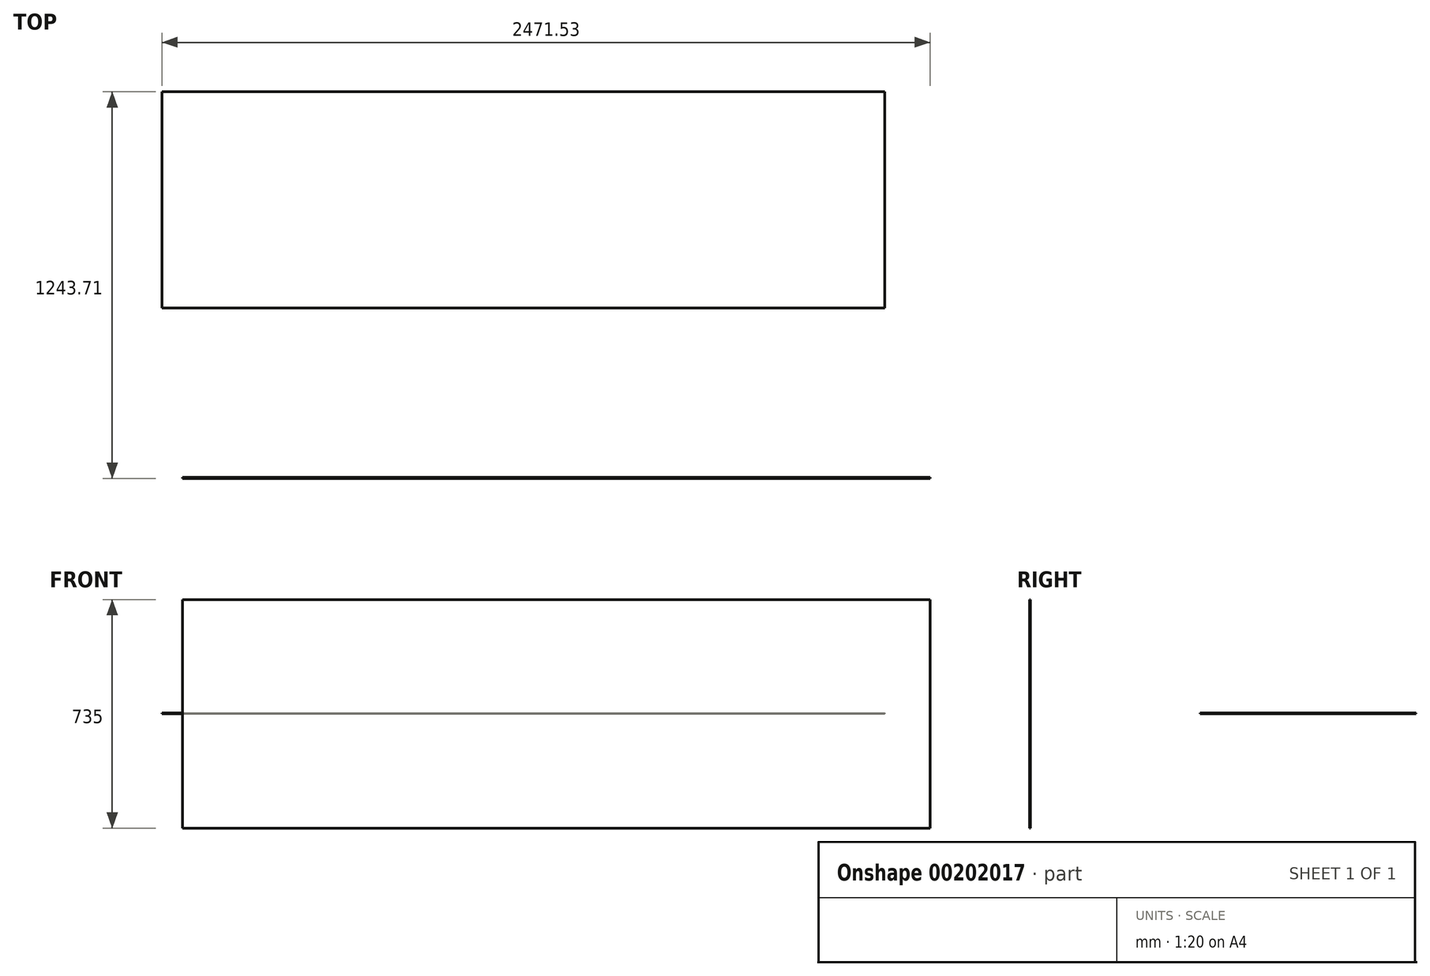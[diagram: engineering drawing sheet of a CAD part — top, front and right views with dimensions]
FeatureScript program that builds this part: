
annotation { "Feature Type Name" : "Feature", "Feature Type Description" : "" }
export const myFeature = defineFeature(function(context is Context, id is Id, definition is map)
    precondition{}
    {
        {
            var Q0;
            Q0=qCreatedBy(makeId("Front.planeOp"),FACE);
            var sketch = newSketch(context, id + "F0", { "sketchPlane" : qUnion([Q0])});
            skLineSegment(sketch, "E0.bottom", {"start": v(1202.5, 367.5) * mm, "end": v(-1202.5, 367.5) * mm});
            skLineSegment(sketch, "E0.top", {"start": v(1202.5, -367.5) * mm, "end": v(-1202.5, -367.5) * mm});
            skLineSegment(sketch, "E0.left", {"start": v(1202.5, 367.5) * mm, "end": v(1202.5, -367.5) * mm});
            skLineSegment(sketch, "E0.right", {"start": v(-1202.5, 367.5) * mm, "end": v(-1202.5, -367.5) * mm});
            skPoint(sketch, "E0.middle", {"position": v(0, 0) * mm});
            skSolve(sketch);
        }
        {
            var Q0;
            Q0=makeQuery(id+"F0.imprint","IMPRINT",FACE,{"disambiguationData":[TD([[makeQuery(id+"F0.imprint","IMPRINT",EDGE,{"derivedFrom":sQuery(id+"F0.wireOp",EDGE,"E0.bottom")}),1.0]])]});
            extrude(context, id + "F1", {"entities" : qUnion([Q0]), "depth" : 3 * mm});
        }
        {
            var Q0;
            Q0=makeQuery(id+"F1.opExtrude","CAP_FACE",FACE,{"disambiguationData":[OSD([sQuery(id+"F0.wireOp",EDGE,"E0.bottom"),sQuery(id+"F0.wireOp",EDGE,"E0.top"),sQuery(id+"F0.wireOp",EDGE,"E0.left"),sQuery(id+"F0.wireOp",EDGE,"E0.right")])],"isStart":false});
            var sketch = newSketch(context, id + "F2", { "sketchPlane" : qUnion([Q0])});
            skLineSegment(sketch, "E1", {"start": v(-1202.5, 17.5) * mm, "end": v(1202.5, 17.5) * mm, "construction": true});
            skPoint(sketch, "E2", {"position": v(0, 17.5) * mm});
            skPoint(sketch, "E3", {"position": v(-1002.5, 17.5) * mm});
            skPoint(sketch, "E4", {"position": v(702.5, 17.5) * mm});
            skLineSegment(sketch, "E5", {"start": v(-1202.5, -17.5) * mm, "end": v(1202.5, -17.5) * mm, "construction": true});
            skPoint(sketch, "E6", {"position": v(-1002.5, -17.5) * mm});
            skPoint(sketch, "E7", {"position": v(0, -17.5) * mm});
            skPoint(sketch, "E8", {"position": v(702.5, -17.5) * mm});
            skSolve(sketch);
        }
        {
            var Q0;
            Q0=makeQuery(id+"F1.opExtrude","CAP_FACE",FACE,{"disambiguationData":[OSD([sQuery(id+"F0.wireOp",EDGE,"E0.bottom"),sQuery(id+"F0.wireOp",EDGE,"E0.top"),sQuery(id+"F0.wireOp",EDGE,"E0.left"),sQuery(id+"F0.wireOp",EDGE,"E0.right")])],"isStart":true});
            var sketch = newSketch(context, id + "F3", { "sketchPlane" : qUnion([Q0])});
            skPoint(sketch, "E9.0", {"position": v(-702.5, 17.5) * mm});
            skPoint(sketch, "E10.0", {"position": v(0, 17.5) * mm});
            skPoint(sketch, "E11.0", {"position": v(1002.5, 17.5) * mm});
            skSolve(sketch);
        }
        {
            var Q0;
            Q0=qCreatedBy(makeId("Top.planeOp"),FACE);
            var sketch = newSketch(context, id + "F4", { "sketchPlane" : qUnion([Q0])});
            skLineSegment(sketch, "E12.bottom", {"start": v(-1269.03, 45.7) * mm, "end": v(1055.97, 45.7) * mm});
            skLineSegment(sketch, "E12.top", {"start": v(-1269.03, 740.7) * mm, "end": v(1055.97, 740.7) * mm});
            skLineSegment(sketch, "E12.left", {"start": v(-1269.03, 45.7) * mm, "end": v(-1269.03, 740.7) * mm});
            skLineSegment(sketch, "E12.right", {"start": v(1055.97, 45.7) * mm, "end": v(1055.97, 740.7) * mm});
            skSolve(sketch);
        }
        {
            var Q0;
            Q0=makeQuery(id+"F4.imprint","IMPRINT",FACE,{"disambiguationData":[TD([[makeQuery(id+"F4.imprint","IMPRINT",EDGE,{"derivedFrom":sQuery(id+"F4.wireOp",EDGE,"E12.bottom")}),1.0]])]});
            extrude(context, id + "F5", {"entities" : qUnion([Q0]), "depth" : 3 * mm});
        }
        {
            var Q0;
            Q0=makeQuery(id+"F5.opExtrude","SWEPT_BODY",BODY,{"disambiguationData":[OSD([sQuery(id+"F4.wireOp",EDGE,"E12.bottom"),sQuery(id+"F4.wireOp",EDGE,"E12.top"),sQuery(id+"F4.wireOp",EDGE,"E12.left"),sQuery(id+"F4.wireOp",EDGE,"E12.right")])]});
            transform(context, id + "F6", {"entities" : qUnion([Q0]), "transformType" : TransformType.TRANSLATION_3D, "dx" : 0 * mm, "dy" : 500 * mm, "dz" : 0 * mm, "makeCopy" : false});
        }
        {
            var Q0;
            Q0=makeQuery(id+"F5.opExtrude","CAP_FACE",FACE,{"disambiguationData":[OSD([sQuery(id+"F4.wireOp",EDGE,"E12.bottom"),sQuery(id+"F4.wireOp",EDGE,"E12.top"),sQuery(id+"F4.wireOp",EDGE,"E12.left"),sQuery(id+"F4.wireOp",EDGE,"E12.right")])],"isStart":false});
            var sketch = newSketch(context, id + "F7", { "sketchPlane" : qUnion([Q0])});
            skLineSegment(sketch, "E13", {"start": v(1055.97, 930.7) * mm, "end": v(-1269.03, 930.7) * mm, "construction": true});
            skPoint(sketch, "E14", {"position": v(-1109.03, 930.7) * mm});
            skPoint(sketch, "E15", {"position": v(-106.53, 930.7) * mm});
            skPoint(sketch, "E16", {"position": v(555.97, 930.7) * mm});
            skSolve(sketch);
        }
    });
